# Revit family: DG 1008 SAY
name_source: partatom
category: Lighting Fixtures
units: mm (PartAtom-declared; Revit-internal decimal feet)

## family parameters
Always vertical = Yes
Classification Number = 23.80.70.11
Cut with Voids When Loaded = No
Host = Ceiling
Light Source = Yes
Maintain Annotation Orientation = No
Part Type = Normal
Room Calculation Point = No
Round Connector Dimension = Use Diameter
Shared = No

## types (18) — shared parameters
Color Filter = 16777215
Dimming Lamp Color Temperature Shift = <None>
Emit Shape Visible in Rendering = Yes
Emit from Circle Diameter = 65 mm  [stored 0.213255 ft]
Manufacturer = ARLIGHT
Tilt Angle = 90.00°
Type Image = DG 1008 SAY.jpg
zero-valued in all types: Default Elevation

## per-type parameters (varying)
| type | Apparent Power | Photometric Web File | Type Comments | Wattage Comments |
| DGSAY.080.8.30.25 | 8 VA | dg1008say-7w-3k-80ra-25d.ies | 8W 25° 3000K | 8W |
| DGSAY.080.8.40.25 | 8 VA | dg1008say-7w-4k-80ra-25d.ies | 8W 25° 4000K | 8W |
| DGSAY.080.8.30.35 | 8 VA | dg1008say-7w-3k-80ra-35d.ies | 8W 35° 3000K | 8W |
| DGSAY.080.8.40.35 | 8 VA | dg1008say-7w-4k-80ra-35d.ies | 8W 35° 4000K | 8W |
| DGSAY.080.8.30.60 | 8 VA | dg10108say-7w-3k-80ra-60d.ies | 8W 60° 3000K | 8 |
| DGSAY.080.8.40.60 | 8 VA | dg1008say-7w-4k-80ra-60d.ies | 8W 60° 4000K | 8W |
| DGSAY.080.6.30.25 | 6 VA | dg1008say-5w-3k-80ra-25d.ies | 6W 25°  3000K | 6W |
| DGSAY.080.6.40.25 | 6 VA | dg1008say-5w-4k-80ra-25d.ies | 6W 25°  4000K | 6W |
| DGSAY.080.6.30.35 | 6 VA | dg1008say-5w-3k-80ra-35d.ies | 6W 25°  3000K | 6W |
| DGSAY.080.6.40.35 | 5 VA | dg1008say-5w-4k-80ra-35d.ies | 6W 35°  4000K | 6W |
| DGSAY.080.6.30.60 | 6 VA | dg1008say-5w-3k-80ra-60d.ies | 6W 60°  3000K | 6W |
| DGSAY.080.6.40.60 | 5 VA | dg1008say-5w-4k-80ra-60d.ies | 6W 60°  4000K | 6W |
| DGSAY.080.11.30.25 | 11 VA | dg1008say-11w-3k-80ra-25d.ies | 11W 25° 3000K | 11W |
| DGSAY.080.11.40.25 | 11 VA | dg1008say-11w-4k-80ra-25d.ies | 11W 25° 4000K | 11W |
| DGSAY.080.11.30.35 | 11 VA | dg1008say-11w-3k-80ra-35d.ies | 11W 35° 3000K | 11W |
| DGSAY.080.11.40.35 | 11 VA | dg1008say-11w-4k-80ra-35d.ies | 11W 35° 4000K | 11W |
| DGSAY.080.11.30.60 | 11 VA | dg1008say-11w-3k-80ra-60d.ies | 11W 60° 3000K | 11W |
| DGSAY.080.11.40.60 | 11 VA | dg1008say-11w-4k-80ra-60d.ies | 11W 60° 4000K | 11W |

note: [stored X ft] marks values corroborated as IEEE doubles in the binary element streams (Revit-internal decimal feet)

## geometry (parser evidence)
native form markers: Sweep x2
no freeform markers — native parametric forms only
